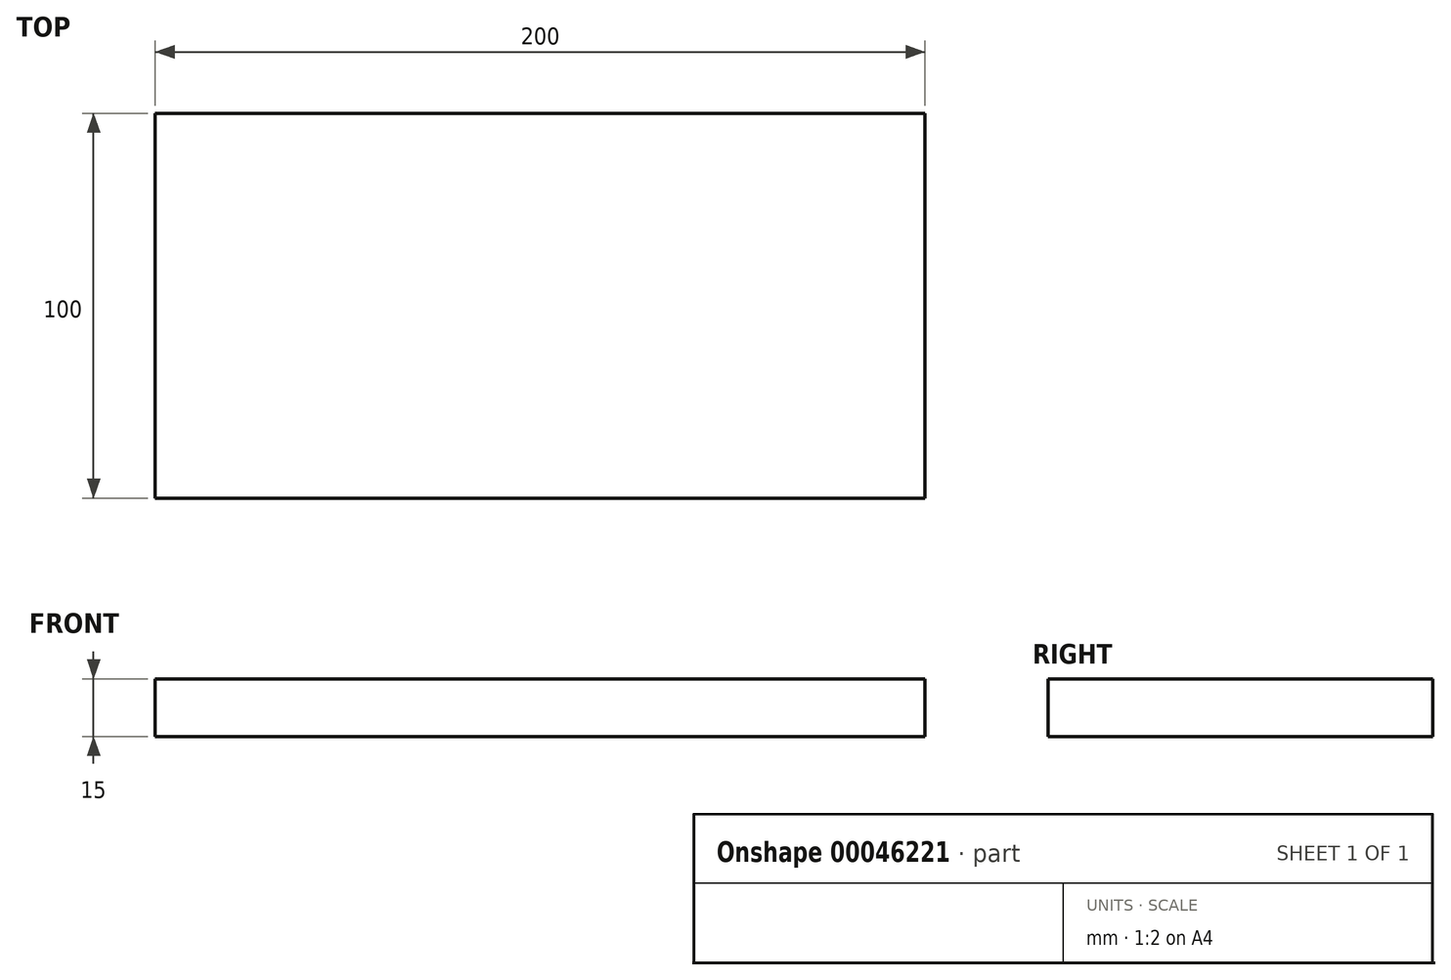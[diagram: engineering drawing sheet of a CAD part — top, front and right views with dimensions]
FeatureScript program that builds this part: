
annotation { "Feature Type Name" : "Feature", "Feature Type Description" : "" }
export const myFeature = defineFeature(function(context is Context, id is Id, definition is map)
    precondition{}
    {
        {
            var Q0;
            Q0=qCreatedBy(makeId("Top.planeOp"),FACE);
            var sketch = newSketch(context, id + "F0", { "sketchPlane" : qUnion([Q0])});
            skLineSegment(sketch, "E0.rect.bottom", {"start": v(100, 50) * mm, "end": v(-100, 50) * mm});
            skLineSegment(sketch, "E0.rect.top", {"start": v(100, -50) * mm, "end": v(-100, -50) * mm});
            skLineSegment(sketch, "E0.rect.left", {"start": v(100, 50) * mm, "end": v(100, -50) * mm});
            skLineSegment(sketch, "E0.rect.right", {"start": v(-100, 50) * mm, "end": v(-100, -50) * mm});
            skPoint(sketch, "E0.rect.middle", {"position": v(0, 0) * mm});
            skSolve(sketch);
        }
        {
            var Q0;
            Q0=makeQuery(id+"F0.imprint","IMPRINT",FACE,{"disambiguationData":[TD([[makeQuery(id+"F0.imprint","IMPRINT",EDGE,{"derivedFrom":sQuery(id+"F0.wireOp",EDGE,"E0.rect.bottom")}),1.0]])]});
            extrude(context, id + "F1", {"entities" : qUnion([Q0]), "oppositeDirection" : true, "depth" : 15 * mm});
        }
        {
            var Q0;
            Q0=makeQuery(id+"F1.opExtrude","SWEPT_FACE",FACE,{"disambiguationData":[OSD([sQuery(id+"F0.wireOp",EDGE,"E0.rect.top")])]});
            cPlane(context, id + "F2", {"entities" : qUnion([Q0]), "cplaneType" : CPlaneType.OFFSET, "offset" : 15 * mm, "oppositeDirection" : true, "width" : 150 * mm, "height" : 150 * mm});
        }
    });
